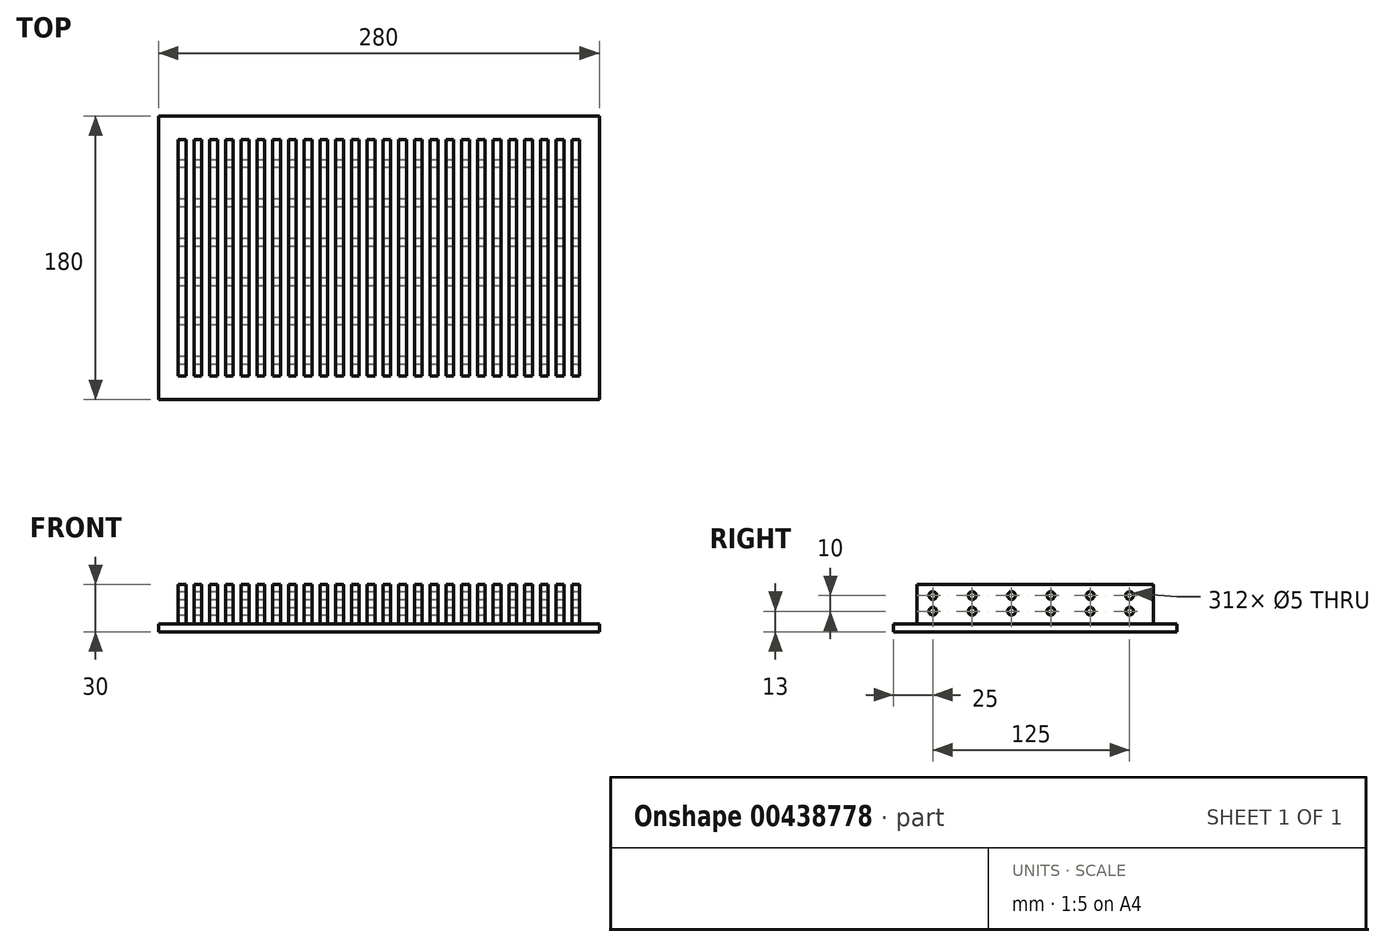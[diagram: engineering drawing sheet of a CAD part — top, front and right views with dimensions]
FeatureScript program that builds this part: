
annotation { "Feature Type Name" : "Feature", "Feature Type Description" : "" }
export const myFeature = defineFeature(function(context is Context, id is Id, definition is map)
    precondition{}
    {
        {
            var Q0;
            Q0=qCreatedBy(makeId("Front.planeOp"),FACE);
            var sketch = newSketch(context, id + "F0", { "sketchPlane" : qUnion([Q0])});
            skLineSegment(sketch, "E0.bottom", {"start": v(140, 2.5) * mm, "end": v(-140, 2.5) * mm});
            skLineSegment(sketch, "E0.top", {"start": v(140, -2.5) * mm, "end": v(-140, -2.5) * mm});
            skLineSegment(sketch, "E0.left", {"start": v(140, 2.5) * mm, "end": v(140, -2.5) * mm});
            skLineSegment(sketch, "E0.right", {"start": v(-140, 2.5) * mm, "end": v(-140, -2.5) * mm});
            skPoint(sketch, "E0.middle", {"position": v(0, 0) * mm});
            skLineSegment(sketch, "E1.bottom", {"start": v(-127.5, 2.5) * mm, "end": v(-122.5, 2.5) * mm});
            skLineSegment(sketch, "E1.top", {"start": v(-127.5, 27.5) * mm, "end": v(-122.5, 27.5) * mm});
            skLineSegment(sketch, "E1.left", {"start": v(-127.5, 2.5) * mm, "end": v(-127.5, 27.5) * mm});
            skLineSegment(sketch, "E1.right", {"start": v(-122.5, 2.5) * mm, "end": v(-122.5, 27.5) * mm});
            skLineSegment(sketch, "E2.1.0.0", {"start": v(-112.5, 2.5) * mm, "end": v(-112.5, 27.5) * mm});
            skLineSegment(sketch, "E2.1.0.1", {"start": v(-117.5, 2.5) * mm, "end": v(-112.5, 2.5) * mm});
            skLineSegment(sketch, "E2.1.0.2", {"start": v(-117.5, 2.5) * mm, "end": v(-117.5, 27.5) * mm});
            skLineSegment(sketch, "E2.1.0.3", {"start": v(-117.5, 27.5) * mm, "end": v(-112.5, 27.5) * mm});
            skLineSegment(sketch, "E2.2.0.0", {"start": v(-102.5, 2.5) * mm, "end": v(-102.5, 27.5) * mm});
            skLineSegment(sketch, "E2.2.0.1", {"start": v(-107.5, 2.5) * mm, "end": v(-102.5, 2.5) * mm});
            skLineSegment(sketch, "E2.2.0.2", {"start": v(-107.5, 2.5) * mm, "end": v(-107.5, 27.5) * mm});
            skLineSegment(sketch, "E2.2.0.3", {"start": v(-107.5, 27.5) * mm, "end": v(-102.5, 27.5) * mm});
            skLineSegment(sketch, "E2.3.0.0", {"start": v(-92.5, 2.5) * mm, "end": v(-92.5, 27.5) * mm});
            skLineSegment(sketch, "E2.3.0.1", {"start": v(-97.5, 2.5) * mm, "end": v(-92.5, 2.5) * mm});
            skLineSegment(sketch, "E2.3.0.2", {"start": v(-97.5, 2.5) * mm, "end": v(-97.5, 27.5) * mm});
            skLineSegment(sketch, "E2.3.0.3", {"start": v(-97.5, 27.5) * mm, "end": v(-92.5, 27.5) * mm});
            skLineSegment(sketch, "E2.4.0.0", {"start": v(-82.5, 2.5) * mm, "end": v(-82.5, 27.5) * mm});
            skLineSegment(sketch, "E2.4.0.1", {"start": v(-87.5, 2.5) * mm, "end": v(-82.5, 2.5) * mm});
            skLineSegment(sketch, "E2.4.0.2", {"start": v(-87.5, 2.5) * mm, "end": v(-87.5, 27.5) * mm});
            skLineSegment(sketch, "E2.4.0.3", {"start": v(-87.5, 27.5) * mm, "end": v(-82.5, 27.5) * mm});
            skLineSegment(sketch, "E2.5.0.0", {"start": v(-72.5, 2.5) * mm, "end": v(-72.5, 27.5) * mm});
            skLineSegment(sketch, "E2.5.0.1", {"start": v(-77.5, 2.5) * mm, "end": v(-72.5, 2.5) * mm});
            skLineSegment(sketch, "E2.5.0.2", {"start": v(-77.5, 2.5) * mm, "end": v(-77.5, 27.5) * mm});
            skLineSegment(sketch, "E2.5.0.3", {"start": v(-77.5, 27.5) * mm, "end": v(-72.5, 27.5) * mm});
            skLineSegment(sketch, "E2.6.0.0", {"start": v(-62.5, 2.5) * mm, "end": v(-62.5, 27.5) * mm});
            skLineSegment(sketch, "E2.6.0.1", {"start": v(-67.5, 2.5) * mm, "end": v(-62.5, 2.5) * mm});
            skLineSegment(sketch, "E2.6.0.2", {"start": v(-67.5, 2.5) * mm, "end": v(-67.5, 27.5) * mm});
            skLineSegment(sketch, "E2.6.0.3", {"start": v(-67.5, 27.5) * mm, "end": v(-62.5, 27.5) * mm});
            skLineSegment(sketch, "E2.7.0.0", {"start": v(-52.5, 2.5) * mm, "end": v(-52.5, 27.5) * mm});
            skLineSegment(sketch, "E2.7.0.1", {"start": v(-57.5, 2.5) * mm, "end": v(-52.5, 2.5) * mm});
            skLineSegment(sketch, "E2.7.0.2", {"start": v(-57.5, 2.5) * mm, "end": v(-57.5, 27.5) * mm});
            skLineSegment(sketch, "E2.7.0.3", {"start": v(-57.5, 27.5) * mm, "end": v(-52.5, 27.5) * mm});
            skLineSegment(sketch, "E2.8.0.0", {"start": v(-42.5, 2.5) * mm, "end": v(-42.5, 27.5) * mm});
            skLineSegment(sketch, "E2.8.0.1", {"start": v(-47.5, 2.5) * mm, "end": v(-42.5, 2.5) * mm});
            skLineSegment(sketch, "E2.8.0.2", {"start": v(-47.5, 2.5) * mm, "end": v(-47.5, 27.5) * mm});
            skLineSegment(sketch, "E2.8.0.3", {"start": v(-47.5, 27.5) * mm, "end": v(-42.5, 27.5) * mm});
            skLineSegment(sketch, "E2.9.0.0", {"start": v(-32.5, 2.5) * mm, "end": v(-32.5, 27.5) * mm});
            skLineSegment(sketch, "E2.9.0.1", {"start": v(-37.5, 2.5) * mm, "end": v(-32.5, 2.5) * mm});
            skLineSegment(sketch, "E2.9.0.2", {"start": v(-37.5, 2.5) * mm, "end": v(-37.5, 27.5) * mm});
            skLineSegment(sketch, "E2.9.0.3", {"start": v(-37.5, 27.5) * mm, "end": v(-32.5, 27.5) * mm});
            skLineSegment(sketch, "E2.10.0.0", {"start": v(-22.5, 2.5) * mm, "end": v(-22.5, 27.5) * mm});
            skLineSegment(sketch, "E2.10.0.1", {"start": v(-27.5, 2.5) * mm, "end": v(-22.5, 2.5) * mm});
            skLineSegment(sketch, "E2.10.0.2", {"start": v(-27.5, 2.5) * mm, "end": v(-27.5, 27.5) * mm});
            skLineSegment(sketch, "E2.10.0.3", {"start": v(-27.5, 27.5) * mm, "end": v(-22.5, 27.5) * mm});
            skLineSegment(sketch, "E2.11.0.0", {"start": v(-12.5, 2.5) * mm, "end": v(-12.5, 27.5) * mm});
            skLineSegment(sketch, "E2.11.0.1", {"start": v(-17.5, 2.5) * mm, "end": v(-12.5, 2.5) * mm});
            skLineSegment(sketch, "E2.11.0.2", {"start": v(-17.5, 2.5) * mm, "end": v(-17.5, 27.5) * mm});
            skLineSegment(sketch, "E2.11.0.3", {"start": v(-17.5, 27.5) * mm, "end": v(-12.5, 27.5) * mm});
            skLineSegment(sketch, "E2.12.0.0", {"start": v(-2.5, 2.5) * mm, "end": v(-2.5, 27.5) * mm});
            skLineSegment(sketch, "E2.12.0.1", {"start": v(-7.5, 2.5) * mm, "end": v(-2.5, 2.5) * mm});
            skLineSegment(sketch, "E2.12.0.2", {"start": v(-7.5, 2.5) * mm, "end": v(-7.5, 27.5) * mm});
            skLineSegment(sketch, "E2.12.0.3", {"start": v(-7.5, 27.5) * mm, "end": v(-2.5, 27.5) * mm});
            skLineSegment(sketch, "E2.13.0.0", {"start": v(7.5, 2.5) * mm, "end": v(7.5, 27.5) * mm});
            skLineSegment(sketch, "E2.13.0.1", {"start": v(2.5, 2.5) * mm, "end": v(7.5, 2.5) * mm});
            skLineSegment(sketch, "E2.13.0.2", {"start": v(2.5, 2.5) * mm, "end": v(2.5, 27.5) * mm});
            skLineSegment(sketch, "E2.13.0.3", {"start": v(2.5, 27.5) * mm, "end": v(7.5, 27.5) * mm});
            skLineSegment(sketch, "E2.14.0.0", {"start": v(17.5, 2.5) * mm, "end": v(17.5, 27.5) * mm});
            skLineSegment(sketch, "E2.14.0.1", {"start": v(12.5, 2.5) * mm, "end": v(17.5, 2.5) * mm});
            skLineSegment(sketch, "E2.14.0.2", {"start": v(12.5, 2.5) * mm, "end": v(12.5, 27.5) * mm});
            skLineSegment(sketch, "E2.14.0.3", {"start": v(12.5, 27.5) * mm, "end": v(17.5, 27.5) * mm});
            skLineSegment(sketch, "E2.15.0.0", {"start": v(27.5, 2.5) * mm, "end": v(27.5, 27.5) * mm});
            skLineSegment(sketch, "E2.15.0.1", {"start": v(22.5, 2.5) * mm, "end": v(27.5, 2.5) * mm});
            skLineSegment(sketch, "E2.15.0.2", {"start": v(22.5, 2.5) * mm, "end": v(22.5, 27.5) * mm});
            skLineSegment(sketch, "E2.15.0.3", {"start": v(22.5, 27.5) * mm, "end": v(27.5, 27.5) * mm});
            skLineSegment(sketch, "E2.16.0.0", {"start": v(37.5, 2.5) * mm, "end": v(37.5, 27.5) * mm});
            skLineSegment(sketch, "E2.16.0.1", {"start": v(32.5, 2.5) * mm, "end": v(37.5, 2.5) * mm});
            skLineSegment(sketch, "E2.16.0.2", {"start": v(32.5, 2.5) * mm, "end": v(32.5, 27.5) * mm});
            skLineSegment(sketch, "E2.16.0.3", {"start": v(32.5, 27.5) * mm, "end": v(37.5, 27.5) * mm});
            skLineSegment(sketch, "E2.17.0.0", {"start": v(47.5, 2.5) * mm, "end": v(47.5, 27.5) * mm});
            skLineSegment(sketch, "E2.17.0.1", {"start": v(42.5, 2.5) * mm, "end": v(47.5, 2.5) * mm});
            skLineSegment(sketch, "E2.17.0.2", {"start": v(42.5, 2.5) * mm, "end": v(42.5, 27.5) * mm});
            skLineSegment(sketch, "E2.17.0.3", {"start": v(42.5, 27.5) * mm, "end": v(47.5, 27.5) * mm});
            skLineSegment(sketch, "E2.18.0.0", {"start": v(57.5, 2.5) * mm, "end": v(57.5, 27.5) * mm});
            skLineSegment(sketch, "E2.18.0.1", {"start": v(52.5, 2.5) * mm, "end": v(57.5, 2.5) * mm});
            skLineSegment(sketch, "E2.18.0.2", {"start": v(52.5, 2.5) * mm, "end": v(52.5, 27.5) * mm});
            skLineSegment(sketch, "E2.18.0.3", {"start": v(52.5, 27.5) * mm, "end": v(57.5, 27.5) * mm});
            skLineSegment(sketch, "E2.19.0.0", {"start": v(67.5, 2.5) * mm, "end": v(67.5, 27.5) * mm});
            skLineSegment(sketch, "E2.19.0.1", {"start": v(62.5, 2.5) * mm, "end": v(67.5, 2.5) * mm});
            skLineSegment(sketch, "E2.19.0.2", {"start": v(62.5, 2.5) * mm, "end": v(62.5, 27.5) * mm});
            skLineSegment(sketch, "E2.19.0.3", {"start": v(62.5, 27.5) * mm, "end": v(67.5, 27.5) * mm});
            skLineSegment(sketch, "E2.20.0.0", {"start": v(77.5, 2.5) * mm, "end": v(77.5, 27.5) * mm});
            skLineSegment(sketch, "E2.20.0.1", {"start": v(72.5, 2.5) * mm, "end": v(77.5, 2.5) * mm});
            skLineSegment(sketch, "E2.20.0.2", {"start": v(72.5, 2.5) * mm, "end": v(72.5, 27.5) * mm});
            skLineSegment(sketch, "E2.20.0.3", {"start": v(72.5, 27.5) * mm, "end": v(77.5, 27.5) * mm});
            skLineSegment(sketch, "E2.21.0.0", {"start": v(87.5, 2.5) * mm, "end": v(87.5, 27.5) * mm});
            skLineSegment(sketch, "E2.21.0.1", {"start": v(82.5, 2.5) * mm, "end": v(87.5, 2.5) * mm});
            skLineSegment(sketch, "E2.21.0.2", {"start": v(82.5, 2.5) * mm, "end": v(82.5, 27.5) * mm});
            skLineSegment(sketch, "E2.21.0.3", {"start": v(82.5, 27.5) * mm, "end": v(87.5, 27.5) * mm});
            skLineSegment(sketch, "E2.22.0.0", {"start": v(97.5, 2.5) * mm, "end": v(97.5, 27.5) * mm});
            skLineSegment(sketch, "E2.22.0.1", {"start": v(92.5, 2.5) * mm, "end": v(97.5, 2.5) * mm});
            skLineSegment(sketch, "E2.22.0.2", {"start": v(92.5, 2.5) * mm, "end": v(92.5, 27.5) * mm});
            skLineSegment(sketch, "E2.22.0.3", {"start": v(92.5, 27.5) * mm, "end": v(97.5, 27.5) * mm});
            skLineSegment(sketch, "E2.23.0.0", {"start": v(107.5, 2.5) * mm, "end": v(107.5, 27.5) * mm});
            skLineSegment(sketch, "E2.23.0.1", {"start": v(102.5, 2.5) * mm, "end": v(107.5, 2.5) * mm});
            skLineSegment(sketch, "E2.23.0.2", {"start": v(102.5, 2.5) * mm, "end": v(102.5, 27.5) * mm});
            skLineSegment(sketch, "E2.23.0.3", {"start": v(102.5, 27.5) * mm, "end": v(107.5, 27.5) * mm});
            skLineSegment(sketch, "E2.24.0.0", {"start": v(117.5, 2.5) * mm, "end": v(117.5, 27.5) * mm});
            skLineSegment(sketch, "E2.24.0.1", {"start": v(112.5, 2.5) * mm, "end": v(117.5, 2.5) * mm});
            skLineSegment(sketch, "E2.24.0.2", {"start": v(112.5, 2.5) * mm, "end": v(112.5, 27.5) * mm});
            skLineSegment(sketch, "E2.24.0.3", {"start": v(112.5, 27.5) * mm, "end": v(117.5, 27.5) * mm});
            skLineSegment(sketch, "E2.25.0.0", {"start": v(127.5, 2.5) * mm, "end": v(127.5, 27.5) * mm});
            skLineSegment(sketch, "E2.25.0.1", {"start": v(122.5, 2.5) * mm, "end": v(127.5, 2.5) * mm});
            skLineSegment(sketch, "E2.25.0.2", {"start": v(122.5, 2.5) * mm, "end": v(122.5, 27.5) * mm});
            skLineSegment(sketch, "E2.25.0.3", {"start": v(122.5, 27.5) * mm, "end": v(127.5, 27.5) * mm});
            skLineSegment(sketch, "E2.direction1", {"start": v(-127.5, 2.5) * mm, "end": v(-117.5, 2.5) * mm, "construction": true});
            skSolve(sketch);
        }
        {
            var Q0;
            Q0 = qSketchRegion(id + "F0", true);
            extrude(context, id + "F1", {"entities" : qUnion([Q0]), "endBound" : BoundingType.SYMMETRIC, "depth" : 180 * mm});
        }
        {
            var Q0;
            Q0=qCreatedBy(makeId("Right.planeOp"),FACE);
            var sketch = newSketch(context, id + "F2", { "sketchPlane" : qUnion([Q0])});
            skLineSegment(sketch, "E3.bottom", {"start": v(-90, 27.5) * mm, "end": v(-75, 27.5) * mm});
            skLineSegment(sketch, "E3.top", {"start": v(-90, 2.5) * mm, "end": v(-75, 2.5) * mm});
            skLineSegment(sketch, "E3.left", {"start": v(-90, 27.5) * mm, "end": v(-90, 2.5) * mm});
            skLineSegment(sketch, "E3.right", {"start": v(-75, 27.5) * mm, "end": v(-75, 2.5) * mm});
            skLineSegment(sketch, "E4.MirrorCS", {"start": v(75, 27.5) * mm, "end": v(75, 2.5) * mm});
            skLineSegment(sketch, "E5.MirrorCS", {"start": v(90, 27.5) * mm, "end": v(90, 2.5) * mm});
            skLineSegment(sketch, "E6.MirrorCS", {"start": v(90, 27.5) * mm, "end": v(75, 27.5) * mm});
            skLineSegment(sketch, "E7.MirrorCS", {"start": v(90, 2.5) * mm, "end": v(75, 2.5) * mm});
            skSolve(sketch);
        }
        {
            var Q0;
            Q0 = qSketchRegion(id + "F2", true);
            extrude(context, id + "F3", {"entities" : qUnion([Q0]), "operationType" : NewBodyOperationType.REMOVE, "endBound" : BoundingType.THROUGH_ALL, "depth" : 25 * mm, "hasSecondDirection" : true, "secondDirectionBound" : SecondDirectionBoundingType.THROUGH_ALL, "secondDirectionOppositeDirection" : true, "secondDirectionDepth" : 25 * mm});
        }
        {
            var Q0;
            Q0=qCreatedBy(makeId("Right.planeOp"),FACE);
            var sketch = newSketch(context, id + "F4", { "sketchPlane" : qUnion([Q0])});
            skCircle(sketch, "E8", {"center": v(-65, 20.5) * mm, "radius": 2.5 * mm});
            skCircle(sketch, "E9", {"center": v(-65, 10.5) * mm, "radius": 2.5 * mm});
            skCircle(sketch, "E10.1.0.0", {"center": v(-40, 20.5) * mm, "radius": 2.5 * mm});
            skCircle(sketch, "E10.1.0.1", {"center": v(-40, 10.5) * mm, "radius": 2.5 * mm});
            skCircle(sketch, "E10.2.0.0", {"center": v(-15, 20.5) * mm, "radius": 2.5 * mm});
            skCircle(sketch, "E10.2.0.1", {"center": v(-15, 10.5) * mm, "radius": 2.5 * mm});
            skCircle(sketch, "E10.3.0.0", {"center": v(10, 20.5) * mm, "radius": 2.5 * mm});
            skCircle(sketch, "E10.3.0.1", {"center": v(10, 10.5) * mm, "radius": 2.5 * mm});
            skCircle(sketch, "E10.4.0.0", {"center": v(35, 20.5) * mm, "radius": 2.5 * mm});
            skCircle(sketch, "E10.4.0.1", {"center": v(35, 10.5) * mm, "radius": 2.5 * mm});
            skCircle(sketch, "E10.5.0.0", {"center": v(60, 20.5) * mm, "radius": 2.5 * mm});
            skCircle(sketch, "E10.5.0.1", {"center": v(60, 10.5) * mm, "radius": 2.5 * mm});
            skLineSegment(sketch, "E10.direction1", {"start": v(-65, 20.5) * mm, "end": v(-40, 20.5) * mm, "construction": true});
            skSolve(sketch);
        }
        {
            var Q0;
            Q0 = qSketchRegion(id + "F4", true);
            extrude(context, id + "F5", {"entities" : qUnion([Q0]), "operationType" : NewBodyOperationType.REMOVE, "endBound" : BoundingType.THROUGH_ALL, "oppositeDirection" : true, "depth" : 25 * mm, "hasSecondDirection" : true, "secondDirectionBound" : SecondDirectionBoundingType.THROUGH_ALL, "secondDirectionOppositeDirection" : false, "secondDirectionDepth" : 25 * mm});
        }
    });
